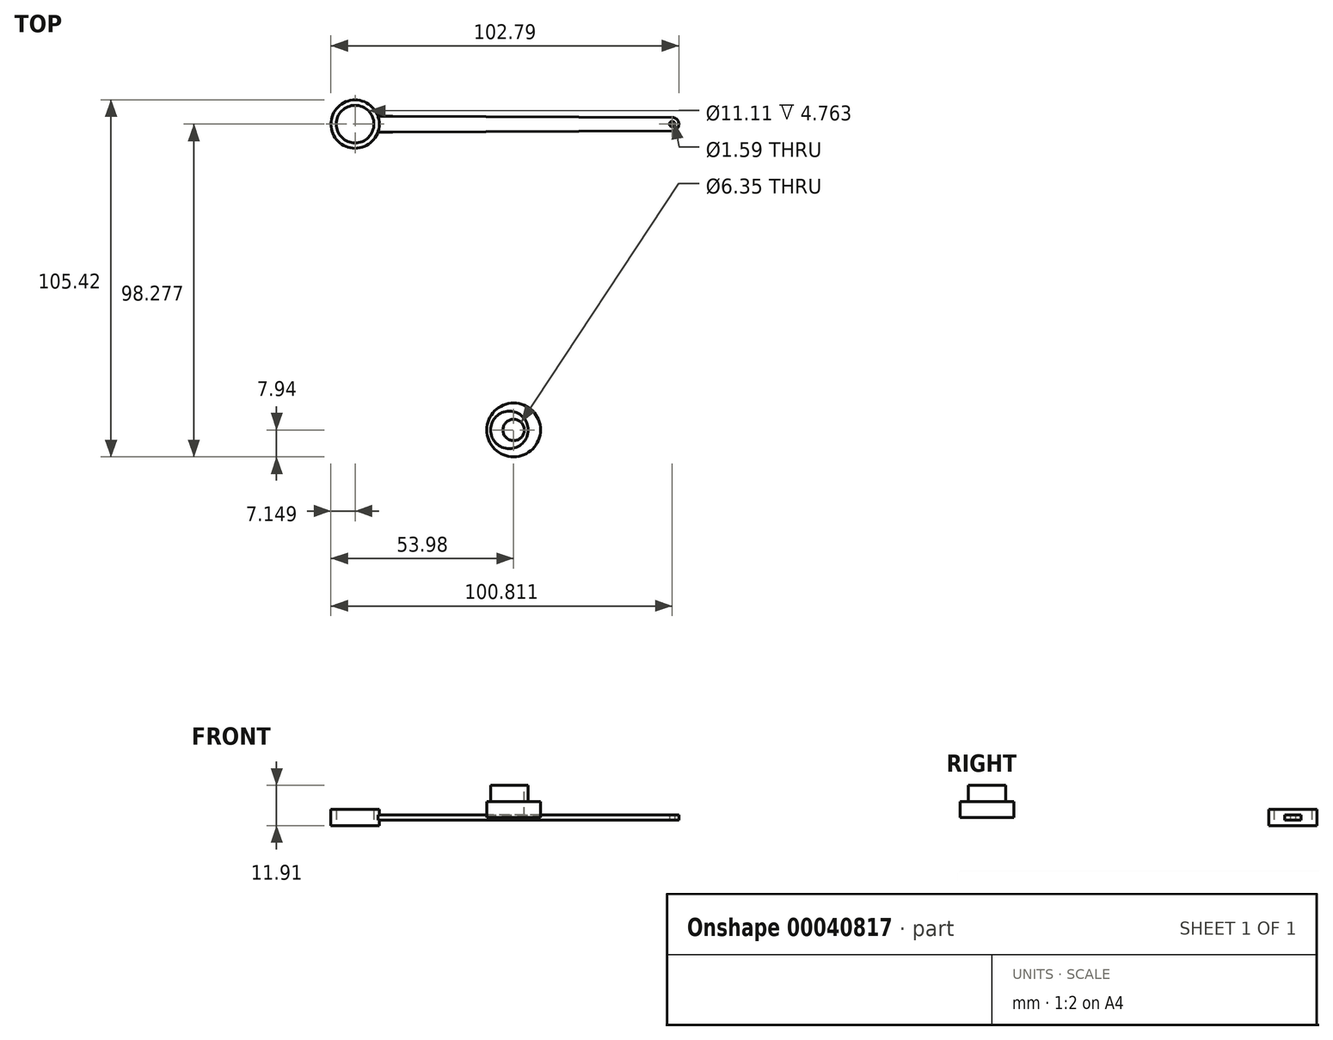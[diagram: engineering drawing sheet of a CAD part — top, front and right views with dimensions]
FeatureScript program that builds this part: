
annotation { "Feature Type Name" : "Feature", "Feature Type Description" : "" }
export const myFeature = defineFeature(function(context is Context, id is Id, definition is map)
    precondition{}
    {
        {
            var Q0;
            Q0=qCreatedBy(makeId("Top.planeOp"),FACE);
            var sketch = newSketch(context, id + "F0", { "sketchPlane" : qUnion([Q0])});
            skCircle(sketch, "E0", {"center": v(-46.83, 0) * mm, "radius": 7.14 * mm});
            skCircle(sketch, "E1", {"center": v(-46.83, 0) * mm, "radius": 5.56 * mm});
            skSolve(sketch);
        }
        {
            var Q0;
            Q0 = qSketchRegion(id + "F0", true);
            extrude(context, id + "F1", {"entities" : qUnion([Q0]), "depth" : 4.76 * mm, "symmetric" : true});
        }
        {
            var Q0;
            Q0=qCreatedBy(makeId("Top.planeOp"),FACE);
            var sketch = newSketch(context, id + "F2", { "sketchPlane" : qUnion([Q0])});
            skCircle(sketch, "E2", {"center": v(46.83, 0) * mm, "radius": 0.8 * mm});
            skLineSegment(sketch, "E3", {"start": v(-35.72, 2.38) * mm, "end": v(46.83, 1.98) * mm});
            skLineSegment(sketch, "E4", {"start": v(46.83, 1.98) * mm, "end": v(46.83, -1.98) * mm, "construction": true});
            skLineSegment(sketch, "E5", {"start": v(46.83, -1.98) * mm, "end": v(-35.72, -2.38) * mm});
            skLineSegment(sketch, "E6.rect.bottom", {"start": v(-35.72, 2.38) * mm, "end": v(-39.69, 2.38) * mm});
            skLineSegment(sketch, "E6.rect.top", {"start": v(-35.72, -2.38) * mm, "end": v(-39.69, -2.38) * mm});
            skLineSegment(sketch, "E6.rect.right", {"start": v(-39.69, 2.38) * mm, "end": v(-39.69, -2.38) * mm, "construction": true});
            skPoint(sketch, "E6.rect.middle", {"position": v(-37.7, 0) * mm});
            skArc(sketch, "E7", {"start": v(46.83, 1.98) * mm, "mid": v(48.8, 0) * mm, "end": v(46.83, -1.98) * mm});
            skLineSegment(sketch, "E8", {"start": v(-35.72, 2.38) * mm, "end": v(-35.72, -2.38) * mm, "construction": true});
            skPoint(sketch, "E9", {"position": v(-35.72, 0) * mm});
            skLineSegment(sketch, "E10.rect.bottom", {"start": v(-39.69, 2.38) * mm, "end": v(-41.06, 2.38) * mm});
            skLineSegment(sketch, "E10.rect.top", {"start": v(-39.69, -2.38) * mm, "end": v(-41.06, -2.38) * mm});
            skLineSegment(sketch, "E10.rect.right", {"start": v(-41.06, 2.38) * mm, "end": v(-41.06, -2.38) * mm});
            skPoint(sketch, "E10.rect.middle", {"position": v(-40.37, 0) * mm});
            skPoint(sketch, "E10.rect.middle.positionSnap0", {"position": v(-39.69, 0) * mm});
            skPoint(sketch, "E10.rect.centerSnap0", {"position": v(-39.69, 0) * mm});
            skSolve(sketch);
        }
        {
            var Q0;
            Q0 = qSketchRegion(id + "F2", true);
            extrude(context, id + "F3", {"entities" : qUnion([Q0]), "operationType" : NewBodyOperationType.ADD, "depth" : 1.59 * mm, "symmetric" : true});
        }
        {
            var Q0;
            Q0=makeQuery(id+"F1.opExtrude","SWEPT_BODY",BODY,{"disambiguationData":[OSD([sQuery(id+"F0.wireOp",EDGE,"E0"),sQuery(id+"F0.wireOp",EDGE,"E1")])]});
            transform(context, id + "F4", {"entities" : qUnion([Q0]), "transformType" : TransformType.TRANSLATION_3D, "dx" : 0 * mm, "dy" : 90.34 * mm, "dz" : 0 * mm, "makeCopy" : false});
        }
        {
            var Q0;
            Q0=qCreatedBy(makeId("Top.planeOp"),FACE);
            var sketch = newSketch(context, id + "F5", { "sketchPlane" : qUnion([Q0])});
            skCircle(sketch, "E11", {"center": v(0, 0) * mm, "radius": 7.94 * mm});
            skSolve(sketch);
        }
        {
            var Q0;
            Q0 = qSketchRegion(id + "F5", true);
            extrude(context, id + "F6", {"entities" : qUnion([Q0]), "depth" : 4.76 * mm});
        }
        {
            var Q0;
            Q0=makeQuery(id+"F6.opExtrude","CAP_FACE",FACE,{"disambiguationData":[OSD([sQuery(id+"F5.wireOp",EDGE,"E11")])],"isStart":false});
            var sketch = newSketch(context, id + "F7", { "sketchPlane" : qUnion([Q0])});
            skCircle(sketch, "E12", {"center": v(-1.27, 0) * mm, "radius": 5.56 * mm});
            skSolve(sketch);
        }
        {
            var Q0;
            Q0 = qSketchRegion(id + "F7", true);
            extrude(context, id + "F8", {"entities" : qUnion([Q0]), "operationType" : NewBodyOperationType.ADD, "depth" : 4.76 * mm});
        }
        {
            var Q0;
            Q0=sQuery(id+"F5.wireOp",VERTEX,"E11.center");
            var Q1;
            Q1=makeQuery(id+"F6.opExtrude","SWEPT_BODY",BODY,{"disambiguationData":[OSD([sQuery(id+"F5.wireOp",EDGE,"E11")])]});
            hole(context, id + "F9", {"style" : HoleStyle.SIMPLE, "holeDiameter" : 6.35 * mm, "endStyle" : HoleEndStyle.THROUGH, "oppositeDirection" : true, "locations" : qUnion([Q0]), "scope" : qUnion([Q1])});
        }
    });
